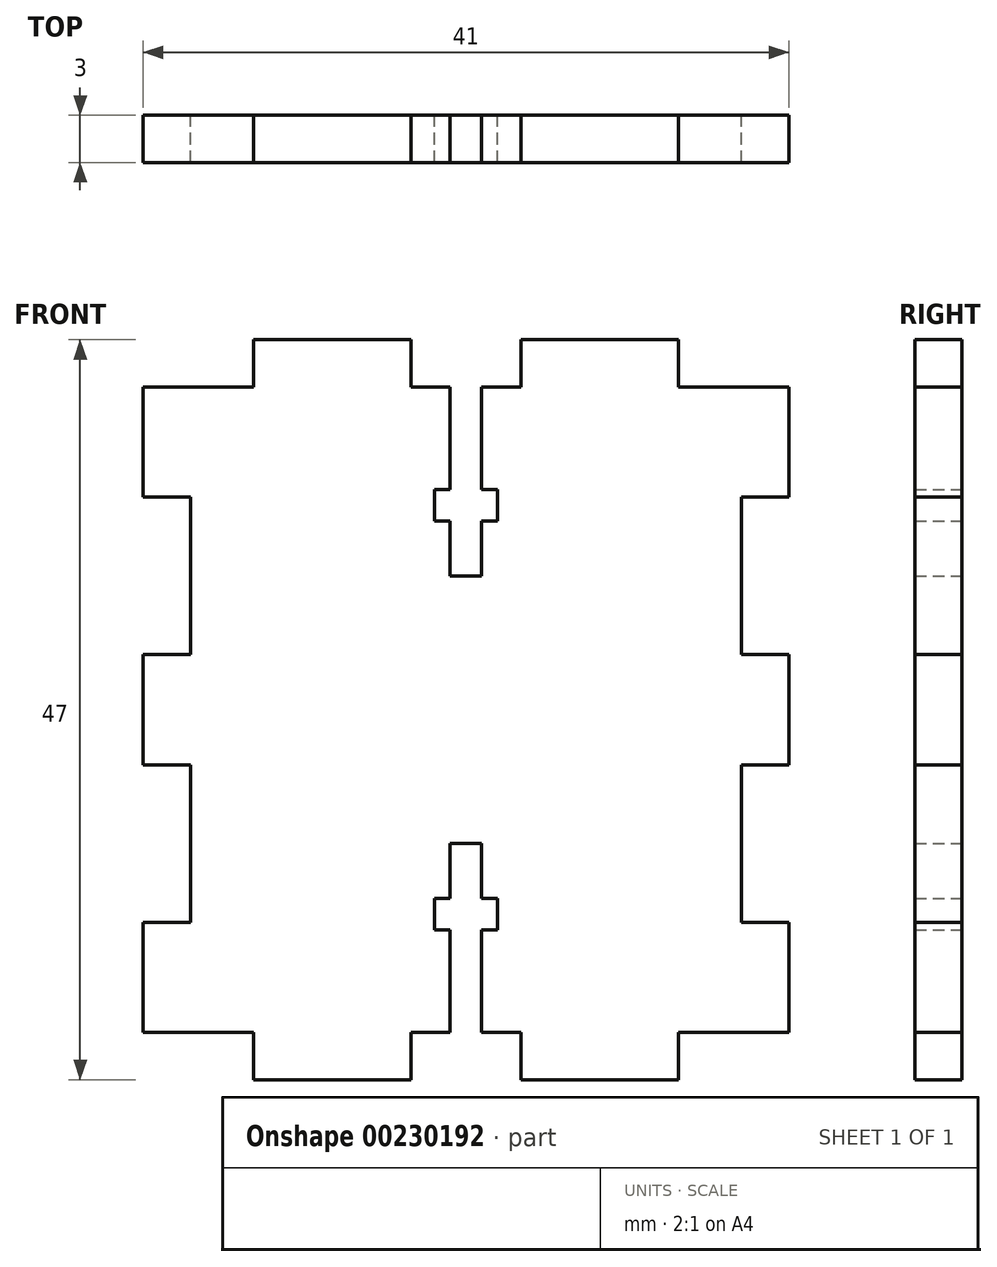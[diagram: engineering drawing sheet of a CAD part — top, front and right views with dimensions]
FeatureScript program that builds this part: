
annotation { "Feature Type Name" : "Feature", "Feature Type Description" : "" }
export const myFeature = defineFeature(function(context is Context, id is Id, definition is map)
    precondition{}
    {
        {
            var Q0;
            Q0=qCreatedBy(makeId("Front.planeOp"),FACE);
            var sketch = newSketch(context, id + "F0", { "sketchPlane" : qUnion([Q0])});
            skLineSegment(sketch, "E0", {"start": v(0, 0) * mm, "end": v(0, 7) * mm});
            skLineSegment(sketch, "E1", {"start": v(0, 7) * mm, "end": v(-3, 7) * mm});
            skLineSegment(sketch, "E2", {"start": v(-3, 7) * mm, "end": v(-3, 17) * mm});
            skLineSegment(sketch, "E3", {"start": v(-3, 17) * mm, "end": v(0, 17) * mm});
            skLineSegment(sketch, "E4", {"start": v(0, 17) * mm, "end": v(0, 24) * mm});
            skLineSegment(sketch, "E5", {"start": v(0, 24) * mm, "end": v(-3, 24) * mm});
            skLineSegment(sketch, "E6", {"start": v(-3, 24) * mm, "end": v(-3, 34) * mm});
            skLineSegment(sketch, "E7", {"start": v(-3, 34) * mm, "end": v(0, 34) * mm});
            skLineSegment(sketch, "E8", {"start": v(0, 34) * mm, "end": v(0, 41) * mm});
            skLineSegment(sketch, "E9", {"start": v(0, 41) * mm, "end": v(-7, 41) * mm});
            skLineSegment(sketch, "E10", {"start": v(-7, 41) * mm, "end": v(-7, 44) * mm});
            skLineSegment(sketch, "E11", {"start": v(-7, 44) * mm, "end": v(-17, 44) * mm});
            skLineSegment(sketch, "E12", {"start": v(-17, 44) * mm, "end": v(-17, 41) * mm});
            skLineSegment(sketch, "E13", {"start": v(-17, 41) * mm, "end": v(-19.5, 41) * mm});
            skLineSegment(sketch, "E14", {"start": v(-19.5, 41) * mm, "end": v(-19.5, 34.5) * mm});
            skLineSegment(sketch, "E15", {"start": v(-19.5, 34.5) * mm, "end": v(-18.5, 34.5) * mm});
            skLineSegment(sketch, "E16", {"start": v(-18.5, 34.5) * mm, "end": v(-18.5, 32.5) * mm});
            skLineSegment(sketch, "E17", {"start": v(-18.5, 32.5) * mm, "end": v(-19.5, 32.5) * mm});
            skLineSegment(sketch, "E18", {"start": v(-19.5, 32.5) * mm, "end": v(-19.5, 29) * mm});
            skLineSegment(sketch, "E19", {"start": v(-19.5, 29) * mm, "end": v(-20.5, 29) * mm});
            skLineSegment(sketch, "E20.MirrorCS", {"start": v(-17, 0) * mm, "end": v(-19.5, 0) * mm});
            skLineSegment(sketch, "E21.MirrorCS", {"start": v(-17, -3) * mm, "end": v(-17, 0) * mm});
            skLineSegment(sketch, "E22.MirrorCS", {"start": v(-7, -3) * mm, "end": v(-17, -3) * mm});
            skLineSegment(sketch, "E23.MirrorCS", {"start": v(-7, 0) * mm, "end": v(-7, -3) * mm});
            skLineSegment(sketch, "E24.MirrorCS", {"start": v(0, 0) * mm, "end": v(-7, 0) * mm});
            skLineSegment(sketch, "E25.MirrorCS", {"start": v(-18.5, 6.5) * mm, "end": v(-18.5, 8.5) * mm});
            skLineSegment(sketch, "E26.MirrorCS", {"start": v(-19.5, 8.5) * mm, "end": v(-19.5, 12) * mm});
            skLineSegment(sketch, "E27.MirrorCS", {"start": v(-19.5, 6.5) * mm, "end": v(-18.5, 6.5) * mm});
            skLineSegment(sketch, "E28.MirrorCS", {"start": v(-18.5, 8.5) * mm, "end": v(-19.5, 8.5) * mm});
            skLineSegment(sketch, "E29.MirrorCS", {"start": v(-19.5, 0) * mm, "end": v(-19.5, 6.5) * mm});
            skLineSegment(sketch, "E30", {"start": v(-19.5, 12) * mm, "end": v(-20.5, 12) * mm});
            skLineSegment(sketch, "E31.MirrorCS", {"start": v(-24, 0) * mm, "end": v(-21.5, 0) * mm});
            skLineSegment(sketch, "E32.MirrorCS", {"start": v(-22.5, 6.5) * mm, "end": v(-22.5, 8.5) * mm});
            skLineSegment(sketch, "E33.MirrorCS", {"start": v(-22.5, 8.5) * mm, "end": v(-21.5, 8.5) * mm});
            skLineSegment(sketch, "E34.MirrorCS", {"start": v(-21.5, 34.5) * mm, "end": v(-22.5, 34.5) * mm});
            skLineSegment(sketch, "E35.MirrorCS", {"start": v(-22.5, 32.5) * mm, "end": v(-21.5, 32.5) * mm});
            skLineSegment(sketch, "E36.MirrorCS", {"start": v(-24, 41) * mm, "end": v(-21.5, 41) * mm});
            skLineSegment(sketch, "E37.MirrorCS", {"start": v(-21.5, 6.5) * mm, "end": v(-22.5, 6.5) * mm});
            skLineSegment(sketch, "E38.MirrorCS", {"start": v(-22.5, 34.5) * mm, "end": v(-22.5, 32.5) * mm});
            skLineSegment(sketch, "E39.MirrorCS", {"start": v(-38, 17) * mm, "end": v(-41, 17) * mm});
            skLineSegment(sketch, "E40.MirrorCS", {"start": v(-41, 0) * mm, "end": v(-34, 0) * mm});
            skLineSegment(sketch, "E41.MirrorCS", {"start": v(-24, -3) * mm, "end": v(-24, 0) * mm});
            skLineSegment(sketch, "E42.MirrorCS", {"start": v(-21.5, 8.5) * mm, "end": v(-21.5, 12) * mm});
            skLineSegment(sketch, "E43.MirrorCS", {"start": v(-21.5, 32.5) * mm, "end": v(-21.5, 29) * mm});
            skLineSegment(sketch, "E44.MirrorCS", {"start": v(-21.5, 0) * mm, "end": v(-21.5, 6.5) * mm});
            skLineSegment(sketch, "E45.MirrorCS", {"start": v(-34, 0) * mm, "end": v(-34, -3) * mm});
            skLineSegment(sketch, "E46.MirrorCS", {"start": v(-34, 41) * mm, "end": v(-34, 44) * mm});
            skLineSegment(sketch, "E47.MirrorCS", {"start": v(-24, 44) * mm, "end": v(-24, 41) * mm});
            skLineSegment(sketch, "E48.MirrorCS", {"start": v(-41, 24) * mm, "end": v(-38, 24) * mm});
            skLineSegment(sketch, "E49.MirrorCS", {"start": v(-41, 17) * mm, "end": v(-41, 24) * mm});
            skLineSegment(sketch, "E50.MirrorCS", {"start": v(-38, 34) * mm, "end": v(-41, 34) * mm});
            skLineSegment(sketch, "E51.MirrorCS", {"start": v(-41, 41) * mm, "end": v(-34, 41) * mm});
            skLineSegment(sketch, "E52.MirrorCS", {"start": v(-41, 7) * mm, "end": v(-38, 7) * mm});
            skLineSegment(sketch, "E53.MirrorCS", {"start": v(-21.5, 41) * mm, "end": v(-21.5, 34.5) * mm});
            skLineSegment(sketch, "E54.MirrorCS", {"start": v(-34, -3) * mm, "end": v(-24, -3) * mm});
            skLineSegment(sketch, "E55.MirrorCS", {"start": v(-41, 34) * mm, "end": v(-41, 41) * mm});
            skLineSegment(sketch, "E56.MirrorCS", {"start": v(-38, 24) * mm, "end": v(-38, 34) * mm});
            skLineSegment(sketch, "E57.MirrorCS", {"start": v(-41, 0) * mm, "end": v(-41, 7) * mm});
            skLineSegment(sketch, "E58.MirrorCS", {"start": v(-34, 44) * mm, "end": v(-24, 44) * mm});
            skLineSegment(sketch, "E59.MirrorCS", {"start": v(-38, 7) * mm, "end": v(-38, 17) * mm});
            skLineSegment(sketch, "E60.MirrorCS", {"start": v(-21.5, 29) * mm, "end": v(-20.5, 29) * mm});
            skLineSegment(sketch, "E61.MirrorCS", {"start": v(-21.5, 12) * mm, "end": v(-20.5, 12) * mm});
            skSolve(sketch);
        }
        {
            var Q0;
            Q0=makeQuery(id+"F0.imprint","IMPRINT",FACE,{"disambiguationData":[TD([[makeQuery(id+"F0.imprint","IMPRINT",EDGE,{"derivedFrom":sQuery(id+"F0.wireOp",EDGE,"E0")}),1.0]])]});
            extrude(context, id + "F1", {"entities" : qUnion([Q0]), "depth" : 3 * mm});
        }
    });
